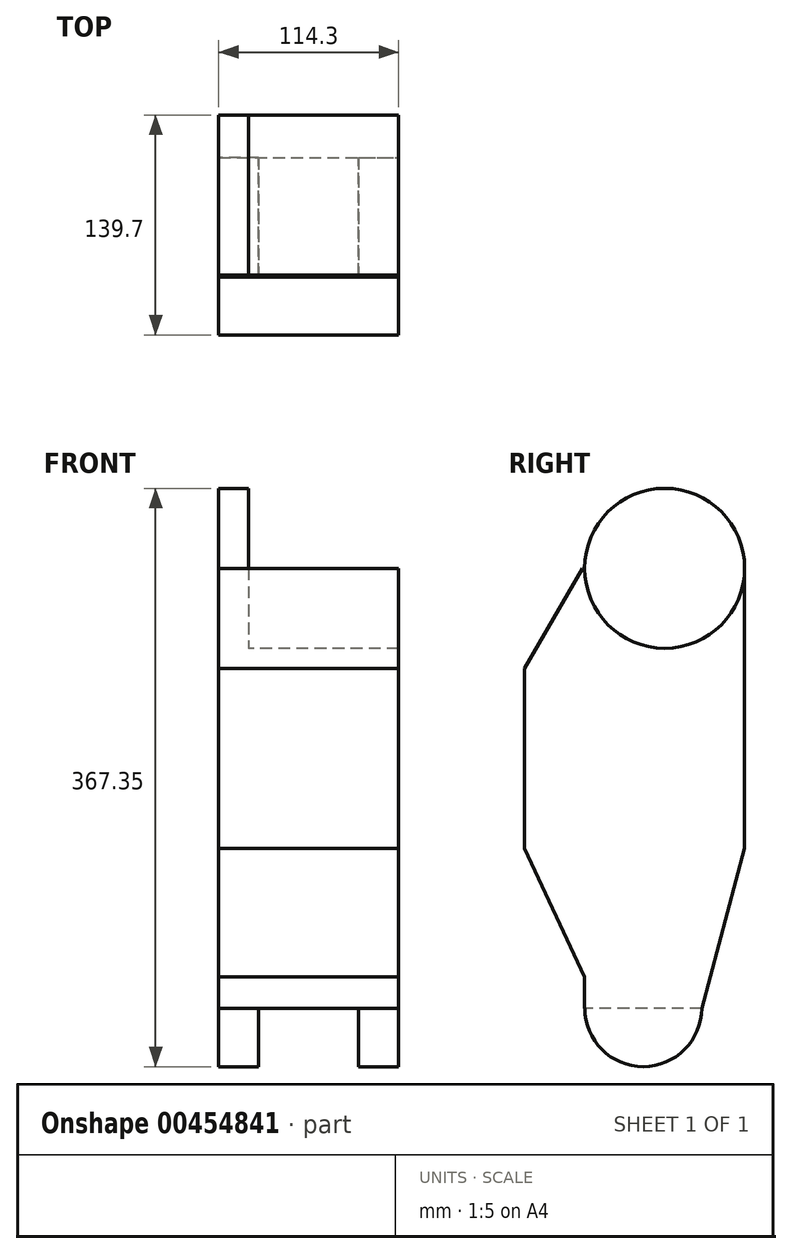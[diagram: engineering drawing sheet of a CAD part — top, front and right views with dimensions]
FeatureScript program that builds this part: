
annotation { "Feature Type Name" : "Feature", "Feature Type Description" : "" }
export const myFeature = defineFeature(function(context is Context, id is Id, definition is map)
    precondition{}
    {
        {
            var Q0;
            Q0=qCreatedBy(makeId("Right.planeOp"),FACE);
            var sketch = newSketch(context, id + "F0", { "sketchPlane" : qUnion([Q0])});
            skCircle(sketch, "E0", {"center": v(0, 0) * mm, "radius": 50.8 * mm});
            skLineSegment(sketch, "E1.bottom", {"start": v(50.8, 0) * mm, "end": v(-50.8, 0) * mm});
            skLineSegment(sketch, "E1.top", {"start": v(50.8, -101.6) * mm, "end": v(-50.8, -101.6) * mm});
            skLineSegment(sketch, "E1.left", {"start": v(50.8, 0) * mm, "end": v(50.8, -101.6) * mm});
            skLineSegment(sketch, "E1.right", {"start": v(-50.8, 0) * mm, "end": v(-50.8, -101.6) * mm});
            skPoint(sketch, "E1.middle", {"position": v(0, -50.8) * mm});
            skSolve(sketch);
        }
        {
            var Q0;
            Q0 = qSketchRegion(id + "F0", true);
            extrude(context, id + "F1", {"entities" : qUnion([Q0]), "depth" : 19.05 * mm, "offsetDistance" : 25.4 * mm});
        }
        {
            var Q0;
            Q0=makeQuery(id+"F0.imprint","IMPRINT",FACE,{"disambiguationData":[TD([[makeQuery(id+"F0.imprint","IMPRINT",EDGE,{"derivedFrom":sQuery(id+"F0.wireOp",EDGE,"E1.top")}),-1.0]])]});
            extrude(context, id + "F2", {"entities" : qUnion([Q0]), "operationType" : NewBodyOperationType.ADD, "depth" : 114.3 * mm, "offsetDistance" : 25.4 * mm});
        }
        {
            var Q0;
            {var subQ0=sQuery(id+"F0.wireOp",EDGE,"E1.top");Q0=makeQuery(id+"F2.boolean.opBoolean","MERGE",FACE,{"derivedFrom":[makeQuery(id+"F1.opExtrude","SWEPT_FACE",FACE,{"disambiguationData":[OSD([subQ0])]}),makeQuery(id+"F2.opExtrude","SWEPT_FACE",FACE,{"disambiguationData":[OSD([subQ0])]})]});}
            var sketch = newSketch(context, id + "F3", { "sketchPlane" : qUnion([Q0])});
            skLineSegment(sketch, "E2.bottom", {"start": v(0, 50.8) * mm, "end": v(114.3, 50.8) * mm});
            skLineSegment(sketch, "E2.top", {"start": v(0, -50.8) * mm, "end": v(114.3, -50.8) * mm});
            skLineSegment(sketch, "E2.left", {"start": v(0, 50.8) * mm, "end": v(0, -50.8) * mm});
            skLineSegment(sketch, "E2.right", {"start": v(114.3, 50.8) * mm, "end": v(114.3, -50.8) * mm});
            skSolve(sketch);
        }
        {
            var Q0;
            Q0 = qSketchRegion(id + "F3", true);
            extrude(context, id + "F4", {"entities" : qUnion([Q0]), "operationType" : NewBodyOperationType.ADD, "depth" : 177.8 * mm, "offsetDistance" : 25.4 * mm});
        }
        {
            var Q0;
            Q0=makeQuery(id+"F4.opExtrude","CAP_EDGE",EDGE,{"disambiguationData":[OSD([sQuery(id+"F3.wireOp",EDGE,"E2.top")])],"isStart":false});
            chamfer(context, id + "F5", {"entities" : qUnion([Q0]), "chamferType" : ChamferType.OFFSET_ANGLE, "width" : 101.6 * mm, "oppositeDirection" : false, "angle" : 15 * degree, "tangentPropagation" : true});
        }
        {
            var Q0;
            Q0=makeQuery(id+"F4.boolean.opBoolean","MERGE",FACE,{"derivedFrom":[makeQuery(id+"F1.opExtrude","CAP_FACE",FACE,{"disambiguationData":[OSD([sQuery(id+"F0.wireOp",EDGE,"E0"),sQuery(id+"F0.wireOp",EDGE,"E1.top"),sQuery(id+"F0.wireOp",EDGE,"E1.left"),sQuery(id+"F0.wireOp",EDGE,"E1.right")])],"isStart":true}),makeQuery(id+"F4.opExtrude","SWEPT_FACE",FACE,{"disambiguationData":[OSD([sQuery(id+"F3.wireOp",EDGE,"E2.left")])]})]});
            var sketch = newSketch(context, id + "F6", { "sketchPlane" : qUnion([Q0])});
            skCircle(sketch, "E3", {"center": v(13.61, -279.4) * mm, "radius": 37.15 * mm});
            skSolve(sketch);
        }
        {
            var Q0;
            Q0 = qSketchRegion(id + "F6", true);
            extrude(context, id + "F7", {"entities" : qUnion([Q0]), "operationType" : NewBodyOperationType.ADD, "oppositeDirection" : true, "depth" : 25.4 * mm, "offsetDistance" : 25.4 * mm});
        }
        {
            var Q0;
            Q0=makeQuery(id+"F4.boolean.opBoolean","MERGE",FACE,{"derivedFrom":[makeQuery(id+"F2.opExtrude","CAP_FACE",FACE,{"disambiguationData":[OSD([sQuery(id+"F0.wireOp",EDGE,"E0"),sQuery(id+"F0.wireOp",EDGE,"E1.top"),sQuery(id+"F0.wireOp",EDGE,"E1.left"),sQuery(id+"F0.wireOp",EDGE,"E1.right")])],"isStart":false}),makeQuery(id+"F4.opExtrude","SWEPT_FACE",FACE,{"disambiguationData":[OSD([sQuery(id+"F3.wireOp",EDGE,"E2.right")])]})]});
            var sketch = newSketch(context, id + "F8", { "sketchPlane" : qUnion([Q0])});
            skCircle(sketch, "E4", {"center": v(-13.61, -279.4) * mm, "radius": 37.15 * mm});
            skSolve(sketch);
        }
        {
            var Q0;
            Q0 = qSketchRegion(id + "F8", true);
            extrude(context, id + "F9", {"entities" : qUnion([Q0]), "operationType" : NewBodyOperationType.ADD, "oppositeDirection" : true, "depth" : 25.4 * mm, "offsetDistance" : 25.4 * mm});
        }
        {
            var Q0;
            {var subQ0=sQuery(id+"F0.wireOp",EDGE,"E1.right");Q0=makeQuery(id+"F4.boolean.opBoolean","MERGE",FACE,{"derivedFrom":[makeQuery(id+"F2.boolean.opBoolean","MERGE",FACE,{"derivedFrom":[makeQuery(id+"F1.opExtrude","SWEPT_FACE",FACE,{"disambiguationData":[OSD([subQ0])]}),makeQuery(id+"F2.opExtrude","SWEPT_FACE",FACE,{"disambiguationData":[OSD([subQ0])]})]}),makeQuery(id+"F4.opExtrude","SWEPT_FACE",FACE,{"disambiguationData":[OSD([sQuery(id+"F3.wireOp",EDGE,"E2.bottom")])]})]});}
            var sketch = newSketch(context, id + "F10", { "sketchPlane" : qUnion([Q0])});
            skLineSegment(sketch, "E5.bottom", {"start": v(0, 0) * mm, "end": v(114.3, 0) * mm});
            skLineSegment(sketch, "E5.top", {"start": v(0, -266.7) * mm, "end": v(114.3, -266.7) * mm});
            skLineSegment(sketch, "E5.left", {"start": v(0, 0) * mm, "end": v(0, -266.7) * mm});
            skLineSegment(sketch, "E5.right", {"start": v(114.3, 0) * mm, "end": v(114.3, -266.7) * mm});
            skSolve(sketch);
        }
        {
            var Q0;
            Q0 = qSketchRegion(id + "F10", true);
            extrude(context, id + "F11", {"entities" : qUnion([Q0]), "operationType" : NewBodyOperationType.ADD, "depth" : 38.1 * mm, "offsetDistance" : 25.4 * mm});
        }
        {
            var Q0;
            Q0=makeQuery(id+"F11.opExtrude","CAP_EDGE",EDGE,{"disambiguationData":[OSD([sQuery(id+"F10.wireOp",EDGE,"E5.top")])],"isStart":false});
            chamfer(context, id + "F12", {"entities" : qUnion([Q0]), "chamferType" : ChamferType.OFFSET_ANGLE, "width" : 88.9 * mm, "oppositeDirection" : false, "angle" : 25 * degree, "tangentPropagation" : true});
        }
        {
            var Q0;
            Q0=makeQuery(id+"F11.opExtrude","CAP_EDGE",EDGE,{"disambiguationData":[OSD([sQuery(id+"F10.wireOp",EDGE,"E5.bottom")])],"isStart":false});
            chamfer(context, id + "F13", {"entities" : qUnion([Q0]), "chamferType" : ChamferType.OFFSET_ANGLE, "width" : 63.5 * mm, "oppositeDirection" : false, "angle" : 30 * degree, "tangentPropagation" : true});
        }
    });
